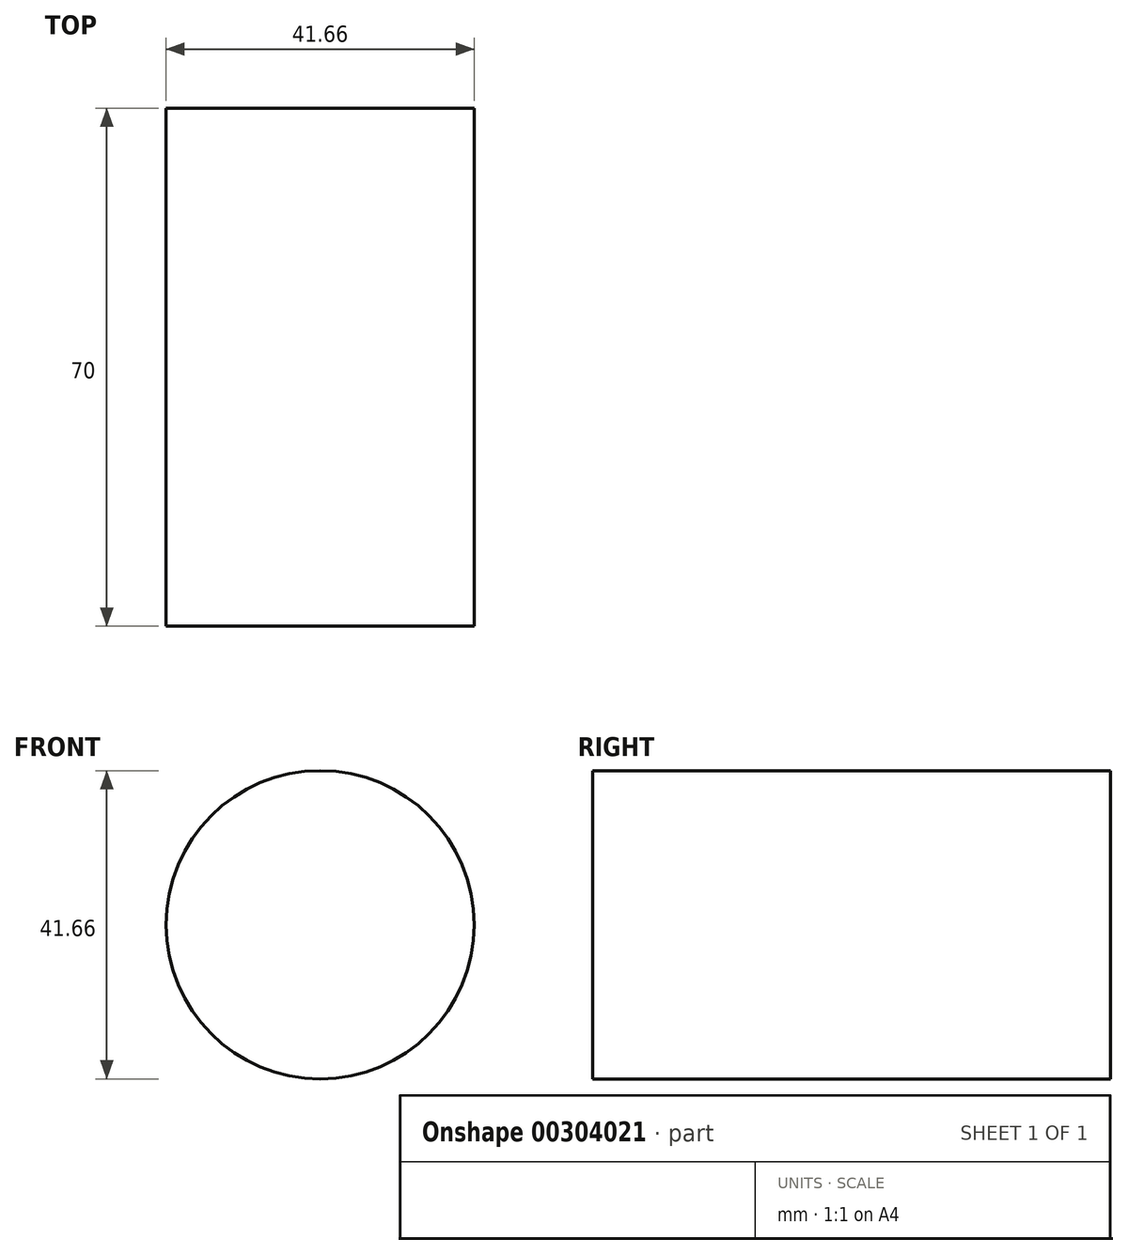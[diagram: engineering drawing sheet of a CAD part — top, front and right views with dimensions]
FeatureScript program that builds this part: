
annotation { "Feature Type Name" : "Feature", "Feature Type Description" : "" }
export const myFeature = defineFeature(function(context is Context, id is Id, definition is map)
    precondition{}
    {
        {
            var Q0;
            Q0=qCreatedBy(makeId("Front.planeOp"),FACE);
            var sketch = newSketch(context, id + "F0", { "sketchPlane" : qUnion([Q0])});
            skCircle(sketch, "E0", {"center": v(0, 0) * mm, "radius": 20.83 * mm});
            skSolve(sketch);
        }
        {
            var Q0;
            Q0 = qSketchRegion(id + "F0", true);
            extrude(context, id + "F1", {"entities" : qUnion([Q0]), "depth" : 70 * mm});
        }
    });
